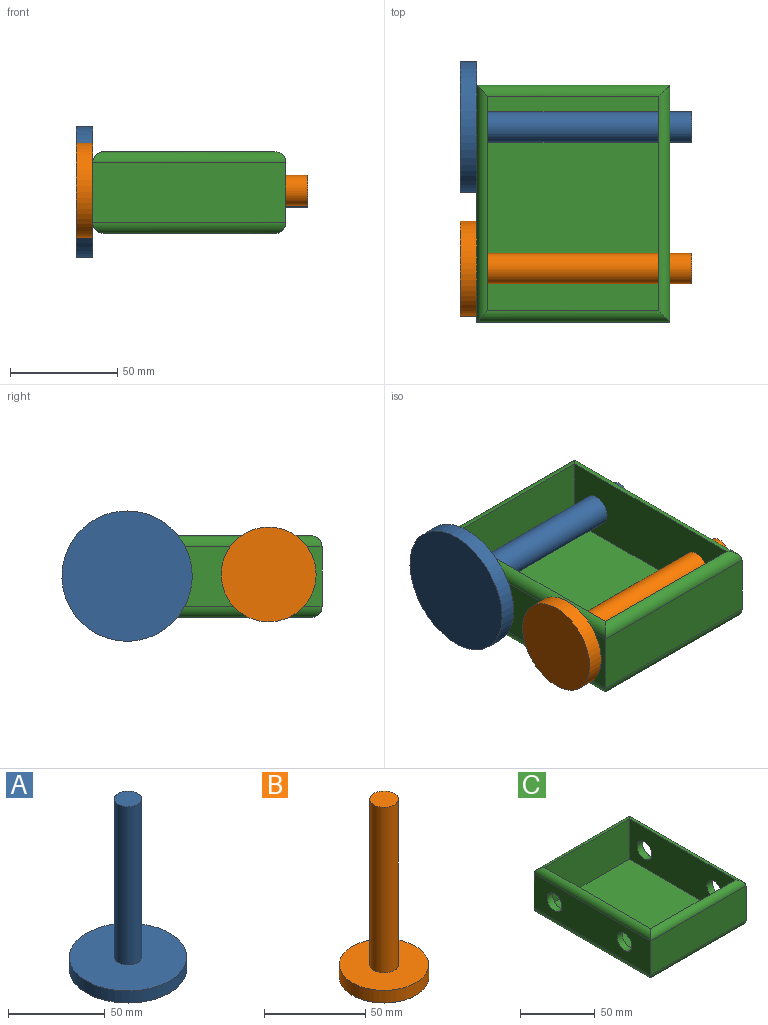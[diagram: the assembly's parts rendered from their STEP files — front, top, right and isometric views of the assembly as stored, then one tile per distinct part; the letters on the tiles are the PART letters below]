
ASSEMBLY  parts=3 mates=3
PART A: 5 faces, bbox 60.7x60.7x107.7 mm
  f0: cylinder r=7.06mm len=100.13mm, axis (0,0,-1), area 4441.7mm2, adj f1,f4
  f1: plane 14.12x14.12mm, normal (0,0,1), area 156.6mm2, adj f0
  f2: cylinder r=30.33mm len=60.67mm, axis (0,0,1), area 1452.3mm2, adj f3,f4
  f3: plane 60.67x60.67mm, normal (0,0,-1), area 2890.7mm2, adj f2
  f4: plane 60.67x60.67mm, normal (0,0,1), area 2734.1mm2, adj f0,f2
PART B: 5 faces, bbox 44.2x44.2x107.7 mm
  f0: cylinder r=7.06mm len=100.13mm, axis (0,0,-1), area 4441.7mm2, adj f1,f4
  f1: plane 14.12x14.12mm, normal (0,0,1), area 156.6mm2, adj f0
  f2: cylinder r=22.1mm len=44.2mm, axis (0,0,1), area 1058.1mm2, adj f3,f4
  f3: plane 44.2x44.2mm, normal (0,0,-1), area 1534.3mm2, adj f2
  f4: plane 44.2x44.2mm, normal (0,0,1), area 1377.7mm2, adj f0,f2
PART C: 22 faces, bbox 90x110.3x38.1 mm
  f0: plane 89.98x27.94mm, normal (0,-1,0), area 2514mm2, adj f1,f3,f14,f18
  f1: plane 110.27x27.94mm, normal (1,0,0), area 2774.3mm2, adj f0,f2,f11,f13,f15,f19
  f2: plane 89.98x27.94mm, normal (0,1,0), area 2514mm2, adj f1,f3,f17,f21
  f3: plane 110.27x27.94mm, normal (-1,0,0), area 2774.3mm2, adj f0,f2,f10,f12,f16,f20
  f4: plane 100.11x79.82mm, normal (0,0,-1), area 7990.5mm2, adj f14,f15,f16,f17
  f5: plane 79.82x33.02mm, normal (0,1,0), area 2635.6mm2, adj f6,f8,f9,f18
  f6: plane 100.11x33.02mm, normal (-1,0,0), area 2999mm2, adj f5,f7,f9,f11,f13,f19
  f7: plane 79.82x33.02mm, normal (0,-1,0), area 2635.6mm2, adj f6,f8,f9,f21
  f8: plane 100.11x33.02mm, normal (1,0,0), area 2999mm2, adj f5,f7,f9,f10,f12,f20
  f9: plane 100.11x79.82mm, normal (0,0,1), area 7990.5mm2, adj f5,f6,f7,f8
  f10: cylinder r=6.99mm len=13.97mm, axis (1,0,0), area 223mm2, adj f3,f8
  f11: cylinder r=6.99mm len=13.97mm, axis (1,0,0), area 223mm2, adj f1,f6
  f12: cylinder r=6.99mm len=13.97mm, axis (1,0,0), area 223mm2, adj f3,f8
  f13: cylinder r=6.99mm len=13.97mm, axis (1,0,0), area 223mm2, adj f1,f6
  f14: cylinder r=5.08mm len=89.98mm, axis (1,0,0), area 688.5mm2, adj f0,f4,f15,f16
  f15: cylinder r=5.08mm len=110.27mm, axis (0,1,0), area 850.4mm2, adj f1,f4,f14,f17
  f16: cylinder r=5.08mm len=110.27mm, axis (0,-1,0), area 850.4mm2, adj f3,f4,f14,f17
  f17: cylinder r=5.08mm len=89.98mm, axis (-1,0,0), area 688.5mm2, adj f2,f4,f15,f16
  f18: cylinder r=5.08mm len=89.98mm, axis (-1,0,0), area 688.5mm2, adj f0,f5,f19,f20
  f19: cylinder r=5.08mm len=110.27mm, axis (0,-1,0), area 850.4mm2, adj f1,f6,f18,f21
  f20: cylinder r=5.08mm len=110.27mm, axis (0,1,0), area 850.4mm2, adj f3,f8,f18,f21
  f21: cylinder r=5.08mm len=89.98mm, axis (1,0,0), area 688.5mm2, adj f2,f7,f19,f20
PLACE A rot(axis=(0.71,0,0.71),180deg) t=(-64.08,41.38,25.35)mm
PLACE B rot(axis=(0.71,0,0.71),180deg) t=(-64.08,-24.57,26.08)mm
PLACE C t=(-19.09,5.71,6.05)mm
MATE parallel B.f0 <-> C.f10  axis (1,0,0) through (-64.08,-24.57,26.08)mm
MATE parallel A.f2 <-> C.f12  axis (1,0,0) through (-64.08,41.38,25.35)mm
MATE parallel C.f10 <-> C.f10  axis (-1,0,0) through (20.82,-24.57,26.08)mm
